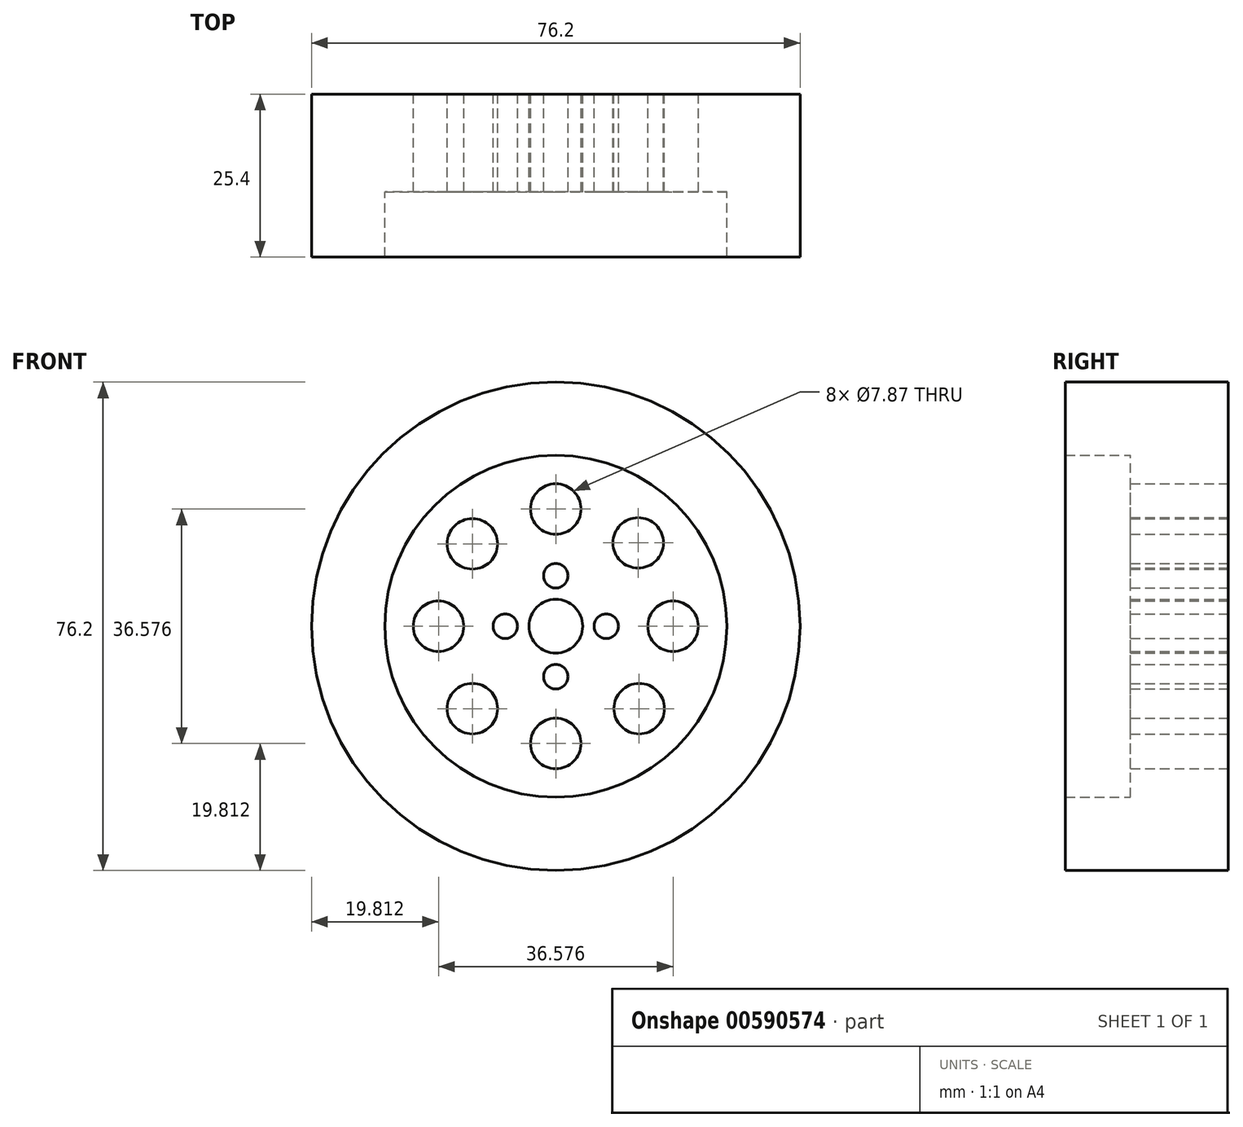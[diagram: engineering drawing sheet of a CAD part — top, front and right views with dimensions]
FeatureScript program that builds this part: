
annotation { "Feature Type Name" : "Feature", "Feature Type Description" : "" }
export const myFeature = defineFeature(function(context is Context, id is Id, definition is map)
    precondition{}
    {
        {
            var Q0;
            Q0=qCreatedBy(makeId("Front.planeOp"),FACE);
            var sketch = newSketch(context, id + "F0", { "sketchPlane" : qUnion([Q0])});
            skCircle(sketch, "E0", {"center": v(0, 0) * mm, "radius": 38.1 * mm});
            skCircle(sketch, "E1", {"center": v(0, 18.29) * mm, "radius": 3.94 * mm});
            skCircle(sketch, "E2", {"center": v(-18.29, 0) * mm, "radius": 3.94 * mm});
            skCircle(sketch, "E3", {"center": v(18.29, 0) * mm, "radius": 3.94 * mm});
            skCircle(sketch, "E4", {"center": v(0, -18.29) * mm, "radius": 3.94 * mm});
            skCircle(sketch, "E5", {"center": v(-13, 12.85) * mm, "radius": 3.94 * mm});
            skCircle(sketch, "E6", {"center": v(12.85, 13) * mm, "radius": 3.94 * mm});
            skCircle(sketch, "E7", {"center": v(13, -12.85) * mm, "radius": 3.94 * mm});
            skCircle(sketch, "E8", {"center": v(-13, -12.85) * mm, "radius": 3.94 * mm});
            skCircle(sketch, "E9", {"center": v(0, -7.87) * mm, "radius": 1.9 * mm});
            skCircle(sketch, "E10", {"center": v(7.87, 0) * mm, "radius": 1.9 * mm});
            skCircle(sketch, "E11", {"center": v(-7.87, 0) * mm, "radius": 1.9 * mm});
            skCircle(sketch, "E12", {"center": v(0, 7.87) * mm, "radius": 1.9 * mm});
            skCircle(sketch, "E13", {"center": v(0, 0) * mm, "radius": 4.2 * mm});
            skCircle(sketch, "E14", {"center": v(0, 0) * mm, "radius": 26.67 * mm});
            skCircle(sketch, "E15", {"center": v(0, 0) * mm, "radius": 36.83 * mm});
            skSolve(sketch);
        }
        {
            var Q0;
            Q0=makeQuery(id+"F0.imprint","IMPRINT",FACE,{"disambiguationData":[TD([[makeQuery(id+"F0.imprint","IMPRINT",EDGE,{"derivedFrom":sQuery(id+"F0.wireOp",EDGE,"E0")}),1.0]])]});
            var Q1;
            Q1=makeQuery(id+"F0.imprint","IMPRINT",FACE,{"disambiguationData":[TD([[makeQuery(id+"F0.imprint","IMPRINT",EDGE,{"derivedFrom":sQuery(id+"F0.wireOp",EDGE,"E14")}),-1.0]])]});
            extrude(context, id + "F1", {"entities" : qUnion([Q0, Q1]), "depth" : 25.4 * mm, "offsetDistance" : 25.4 * mm});
        }
        {
            var Q0;
            Q0=makeQuery(id+"F0.imprint","IMPRINT",FACE,{"disambiguationData":[TD([[makeQuery(id+"F0.imprint","IMPRINT",EDGE,{"derivedFrom":sQuery(id+"F0.wireOp",EDGE,"E1")}),-1.0]])]});
            extrude(context, id + "F2", {"entities" : qUnion([Q0]), "operationType" : NewBodyOperationType.ADD, "depth" : 15.24 * mm, "offsetDistance" : 25.4 * mm});
        }
    });
